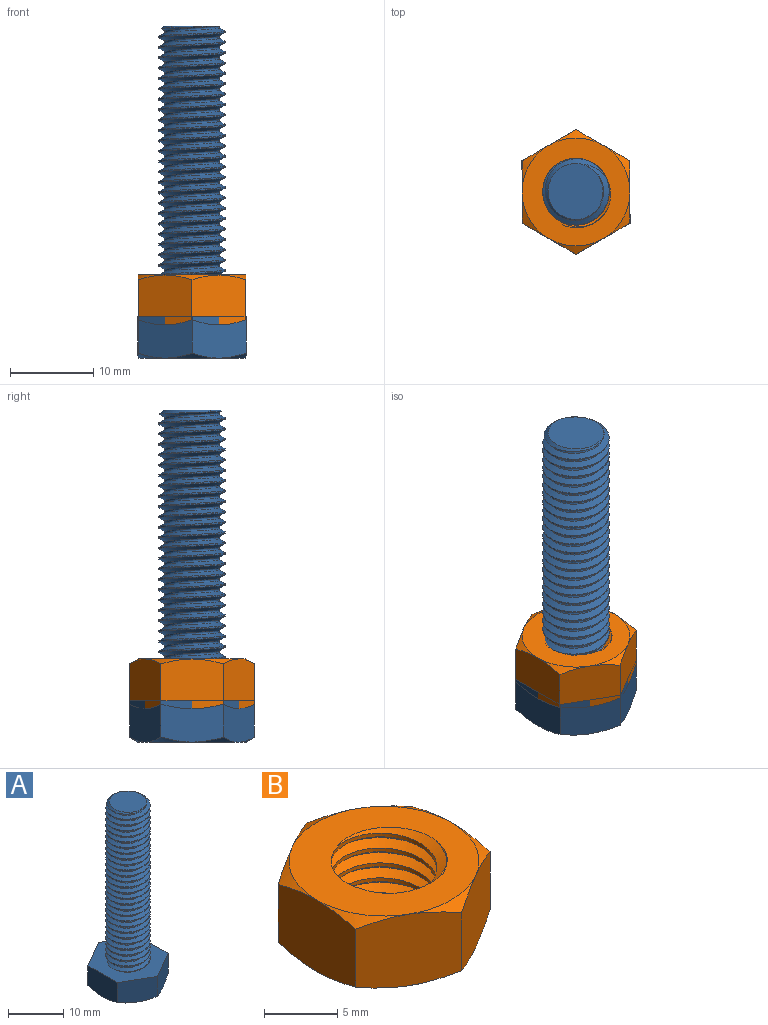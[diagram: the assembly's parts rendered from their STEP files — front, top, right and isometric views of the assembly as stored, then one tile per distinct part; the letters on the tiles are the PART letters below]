
ASSEMBLY  parts=2 mates=1
PART A: 20 faces, bbox 15.5x15.5x41 mm
  f0: cylinder r=4mm len=34.46mm, axis (0,0,-1), area 109.3mm2, adj f8,f17,f18,f19
  f1: plane 7.03x5.52mm, normal (0.5,0.87,0), area 36.1mm2, adj f2,f6,f7,f8,f10,f15
  f2: plane 7.01x5.52mm, normal (-0.5,0.86,0), area 36.1mm2, adj f1,f3,f7,f8,f14,f15
  f3: plane 8.03x5.52mm, normal (-1,0,0), area 36.1mm2, adj f2,f4,f7,f8,f13,f14
  f4: plane 7.03x5.52mm, normal (-0.5,-0.87,0), area 36.1mm2, adj f3,f5,f7,f8,f12,f13
  f5: plane 7.01x5.52mm, normal (0.5,-0.86,0), area 36.1mm2, adj f4,f6,f7,f8,f11,f12
  f6: plane 8.03x5.52mm, normal (1,0,0), area 36.1mm2, adj f1,f5,f7,f8,f10,f11
  f7: plane 13.02x13mm, normal (0,0,-1), area 133.1mm2, adj f1,f2,f3,f4,f5,f6,f10,f11
  f8: plane 15.36x13.36mm, normal (0,0,1), area 105.2mm2, adj f0,f1,f2,f3,f4,f5,f6,f16
  f9: plane 6.79x6.69mm, normal (0,0,1), area 35.2mm2, adj f16,f17,f18,f19
  f10: cone r=8.66mm half-angle=60deg, axis (0,0,1), area 3.7mm2, adj f1,f6,f7
  f11: cone r=8.66mm half-angle=60deg, axis (0,0,1), area 3.7mm2, adj f5,f6,f7
  f12: cone r=8.66mm half-angle=60deg, axis (0,0,1), area 3.7mm2, adj f4,f5,f7
  f13: cone r=8.66mm half-angle=60deg, axis (0,0,1), area 3.7mm2, adj f3,f4,f7
  f14: cone r=8.66mm half-angle=60deg, axis (0,0,1), area 3.7mm2, adj f2,f3,f7
  f15: cone r=8.66mm half-angle=60deg, axis (0,0,1), area 3.7mm2, adj f1,f2,f7
  f16: bspline ~35.94x7.68mm, area 202mm2, adj f8,f9,f17,f18
  f17: bspline ~36.02x9.24mm, area 501mm2, adj f0,f8,f9,f16,f19
  f18: bspline ~35.6x9.24mm, area 500.5mm2, adj f0,f8,f9,f16,f19
  f19: cone r=4mm half-angle=49.1deg, axis (0,0,-1), area 7.8mm2, adj f0,f9,f17,f18
PART B: 24 faces, bbox 15.6x15.6x7.7 mm
  f0: plane 13.34x13.34mm, normal (0,0,1), area 84.1mm2, adj f4,f5,f7,f9,f11,f13,f20,f21
  f1: plane 13.37x13.37mm, normal (0,0,-1), area 84.1mm2, adj f2,f3,f6,f8,f10,f12,f20,f21
  f2: cone r=6.5mm half-angle=60deg, axis (0,0,1), area 4.2mm2, adj f1,f14,f15
  f3: cone r=6.5mm half-angle=60deg, axis (0,0,1), area 4.2mm2, adj f1,f14,f19
  f4: cone r=6.5mm half-angle=60deg, axis (0,0,-1), area 4.2mm2, adj f0,f14,f15
  f5: cone r=6.5mm half-angle=60deg, axis (0,0,-1), area 4.2mm2, adj f0,f14,f19
  f6: cone r=6.5mm half-angle=60deg, axis (0,0,1), area 4.2mm2, adj f1,f15,f16
  f7: cone r=6.5mm half-angle=60deg, axis (0,0,-1), area 4.2mm2, adj f0,f15,f16
  f8: cone r=6.5mm half-angle=60deg, axis (0,0,1), area 4.2mm2, adj f1,f16,f17
  f9: cone r=6.5mm half-angle=60deg, axis (0,0,-1), area 4.2mm2, adj f0,f16,f17
  f10: cone r=6.5mm half-angle=60deg, axis (0,0,1), area 4.2mm2, adj f1,f17,f18
  f11: cone r=6.5mm half-angle=60deg, axis (0,0,-1), area 4.2mm2, adj f0,f17,f18
  f12: cone r=6.5mm half-angle=60deg, axis (0,0,1), area 4.2mm2, adj f1,f18,f19
  f13: cone r=6.5mm half-angle=60deg, axis (0,0,-1), area 4.2mm2, adj f0,f18,f19
  f14: plane 7.12x6.63mm, normal (0.5,-0.87,0), area 42mm2, adj f2,f3,f4,f5,f15,f19
  f15: plane 7.12x6.63mm, normal (-0.5,-0.87,0), area 42mm2, adj f2,f4,f6,f7,f14,f16
  f16: plane 8.13x6.62mm, normal (-1,0,0), area 42mm2, adj f6,f7,f8,f9,f15,f17
  f17: plane 7.12x6.63mm, normal (-0.5,0.87,0), area 42mm2, adj f8,f9,f10,f11,f16,f18
  f18: plane 7.12x6.63mm, normal (0.5,0.87,0), area 42mm2, adj f10,f11,f12,f13,f17,f19
  f19: plane 8.13x6.62mm, normal (1,0,0), area 42mm2, adj f3,f5,f12,f13,f14,f18
  f20: bspline ~9.93x8.6mm, area 93.4mm2, adj f0,f1,f22,f23
  f21: bspline ~9.93x8.6mm, area 93.6mm2, adj f0,f1,f22,f23
  f22: bspline ~10.07x8.72mm, area 23.6mm2, adj f0,f1,f20,f21
  f23: cylinder r=3.62mm len=7.25mm, axis (0,0,1), area 34mm2, adj f0,f1,f20,f21
PLACE A t=(12.16,8.71,-10.19)mm fixed
PLACE B rot(axis=(1,0,0),180deg) t=(12.16,8.71,-0.19)mm
MATE cylindrical B.f23 <-> A.f10  axis (0,0,1) through (12.16,8.71,-0.19)mm
